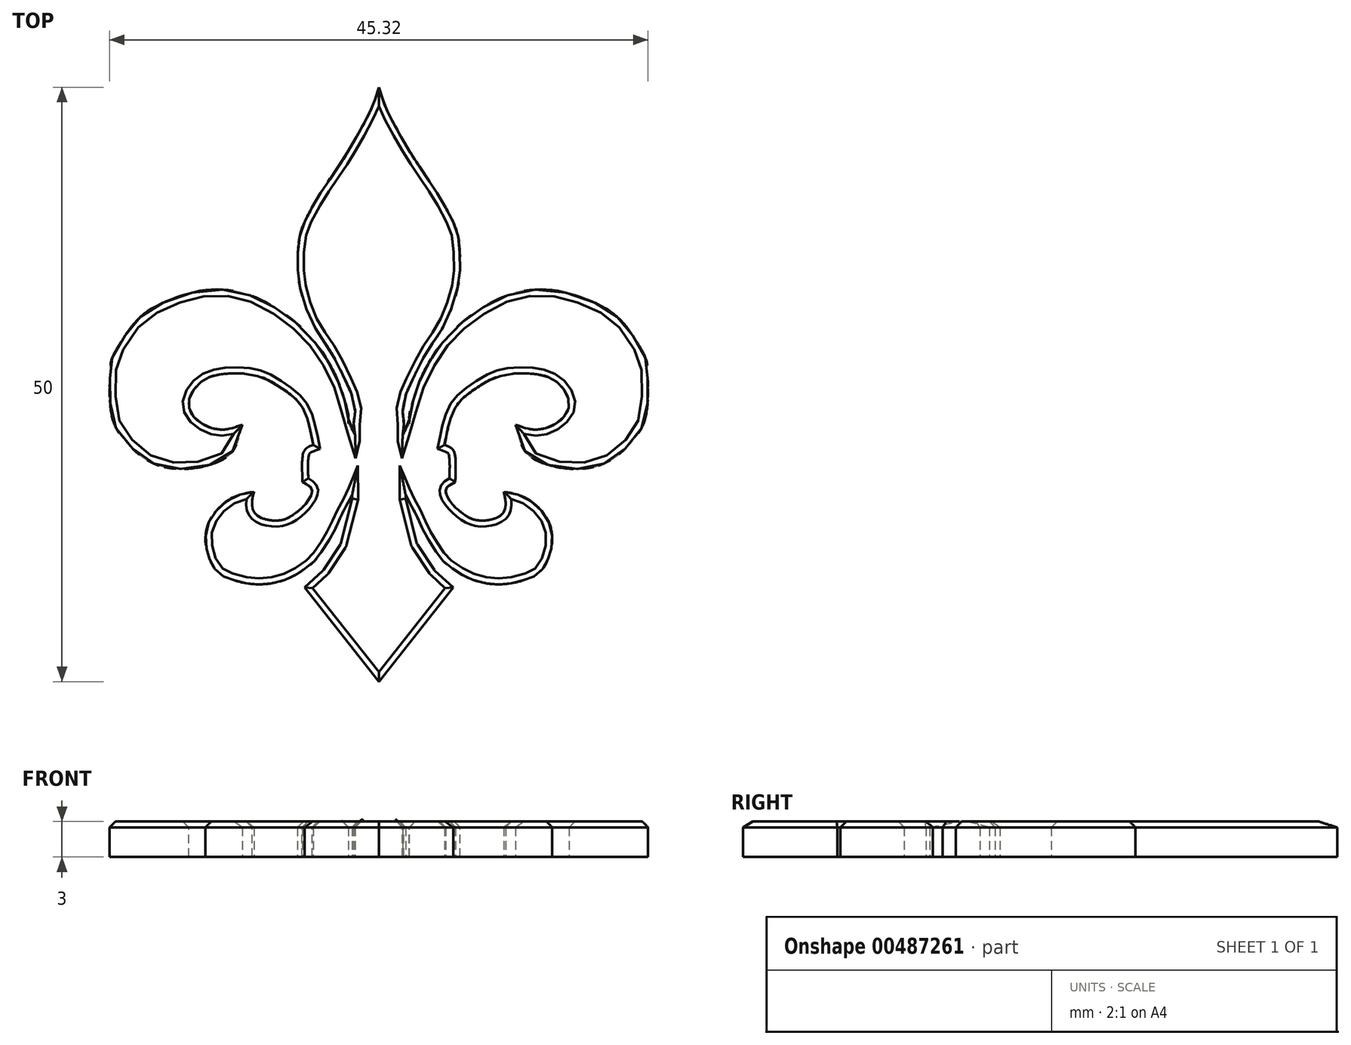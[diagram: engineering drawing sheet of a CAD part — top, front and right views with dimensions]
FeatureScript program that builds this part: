
annotation { "Feature Type Name" : "Feature", "Feature Type Description" : "" }
export const myFeature = defineFeature(function(context is Context, id is Id, definition is map)
    precondition{}
    {
        {
            var Q0;
            Q0=qCreatedBy(makeId("Top.planeOp"),FACE);
            var sketch = newSketch(context, id + "F0", { "sketchPlane" : qUnion([Q0])});
            skFitSpline(sketch, "E0", {"points": [v(11.5, 2.74) * mm, v(13.38, 2.32) * mm, v(15.33, 3.16) * mm, v(16, 4.67) * mm, v(15, 6.3) * mm, v(13.4, 6.96) * mm, v(10.33, 6.88) * mm, v(8.2, 5.81) * mm, v(6.5, 4.3) * mm, v(5.76, 2.22) * mm, v(5.52, 1.03) * mm], "startDerivative": vector(19.3, -6.88) * mm, "endDerivative": vector(-2.82, -13.97) * mm});
            skFitSpline(sketch, "E1", {"points": [v(5.52, 1.03) * mm, v(6.22, 0.64) * mm, v(6.45, -0.33) * mm, v(6.43, -2.09) * mm], "startDerivative": vector(2.93, -1.03) * mm, "endDerivative": vector(-0.17, -4.48) * mm});
            skFitSpline(sketch, "E2", {"points": [v(6.43, -2.09) * mm, v(5.63, -2.72) * mm, v(5.95, -3.63) * mm, v(6.63, -4.4) * mm, v(7.7, -5.13) * mm, v(8.74, -5.33) * mm, v(9.87, -5.1) * mm, v(10.53, -4.56) * mm, v(10.66, -3.7) * mm, v(10.5, -2.9) * mm], "startDerivative": vector(-9.63, -4.74) * mm, "endDerivative": vector(-2.24, 7.58) * mm});
            skFitSpline(sketch, "E3", {"points": [v(11.5, 2.74) * mm, v(12.27, 0.55) * mm, v(13.89, -0.53) * mm, v(16.43, -0.98) * mm, v(18.62, -0.66) * mm, v(20.21, 0.26) * mm, v(21.75, 1.88) * mm, v(22.43, 3.3) * mm, v(22.66, 5.5) * mm, v(22.62, 6.97) * mm, v(22.5, 8.17) * mm, v(21.68, 9.74) * mm, v(20.6, 11.26) * mm, v(19.34, 12.35) * mm, v(17.2, 13.39) * mm, v(14.4, 14.09) * mm, v(11.95, 13.95) * mm, v(9.92, 13.24) * mm, v(8.06, 12.14) * mm, v(6.57, 10.95) * mm, v(5.01, 9.2) * mm, v(4.18, 7.88) * mm, v(3.5, 6.57) * mm, v(3.13, 5.57) * mm, v(2.84, 4.65) * mm, v(2.57, 3.5) * mm, v(2.51, 2.74) * mm, v(2, 1.84) * mm], "startDerivative": vector(14.67, -57.16) * mm, "endDerivative": vector(-10.4, -34.92) * mm});
            skFitSpline(sketch, "E4", {"points": [v(2, 1.84) * mm, v(2.1, 2.74) * mm, v(2, 4.16) * mm, v(3, 6.9) * mm, v(4.22, 9.17) * mm, v(5.48, 11.08) * mm, v(6.66, 14.41) * mm, v(6.83, 16.72) * mm, v(6.61, 18.8) * mm, v(5.94, 20.41) * mm, v(4.88, 22.27) * mm, v(3.75, 23.94) * mm, v(2.72, 25.52) * mm, v(1.54, 27.56) * mm, v(0.82, 28.93) * mm, v(0.42, 29.83) * mm, v(0, 31.12) * mm], "startDerivative": vector(-4.93, 20.4) * mm, "endDerivative": vector(-7.9, 26.17) * mm});
            skFitSpline(sketch, "E5", {"points": [v(10.5, -2.9) * mm, v(12.12, -3.3) * mm, v(13.5, -4.3) * mm, v(14.35, -5.56) * mm, v(14.59, -7.08) * mm, v(14.37, -8.17) * mm, v(14, -9.09) * mm, v(13.3, -9.86) * mm, v(12.33, -10.3) * mm, v(11.2, -10.59) * mm, v(9.94, -10.7) * mm, v(8.46, -10.48) * mm, v(7.29, -10.04) * mm, v(6.42, -9.51) * mm, v(5.49, -8.8) * mm, v(4.78, -7.87) * mm, v(4.05, -6.73) * mm, v(3.45, -5.55) * mm, v(2.93, -4.43) * mm, v(2.25, -3.16) * mm], "startDerivative": vector(27.91, -4.23) * mm, "endDerivative": vector(-9.83, 23.64) * mm});
            skLineSegment(sketch, "E6", {"start": v(2.25, -3.16) * mm, "end": v(2.25, -3.5) * mm});
            skLineSegment(sketch, "E7", {"start": v(2.25, -3.5) * mm, "end": v(3.2, -7.29) * mm});
            skLineSegment(sketch, "E8", {"start": v(3.2, -7.29) * mm, "end": v(4.69, -9.52) * mm});
            skLineSegment(sketch, "E9", {"start": v(4.69, -9.52) * mm, "end": v(6.25, -10.96) * mm});
            skLineSegment(sketch, "E10", {"start": v(6.25, -10.96) * mm, "end": v(0, -18.88) * mm});
            skFitSpline(sketch, "E11.MirrorCS", {"points": [v(-2, 1.84) * mm, v(-2.1, 2.74) * mm, v(-2, 4.16) * mm, v(-3, 6.9) * mm, v(-4.22, 9.17) * mm, v(-5.48, 11.08) * mm, v(-6.66, 14.41) * mm, v(-6.83, 16.72) * mm, v(-6.61, 18.8) * mm, v(-5.94, 20.41) * mm, v(-4.88, 22.27) * mm, v(-3.75, 23.94) * mm, v(-2.72, 25.52) * mm, v(-1.54, 27.56) * mm, v(-0.82, 28.93) * mm, v(-0.42, 29.83) * mm, v(0, 31.12) * mm], "startDerivative": vector(4.93, 20.4) * mm, "endDerivative": vector(7.9, 26.17) * mm});
            skFitSpline(sketch, "E12.MirrorCS", {"points": [v(-11.5, 2.74) * mm, v(-12.27, 0.55) * mm, v(-13.89, -0.53) * mm, v(-16.43, -0.98) * mm, v(-18.62, -0.66) * mm, v(-20.21, 0.26) * mm, v(-21.75, 1.88) * mm, v(-22.43, 3.3) * mm, v(-22.66, 5.5) * mm, v(-22.62, 6.97) * mm, v(-22.5, 8.17) * mm, v(-21.68, 9.74) * mm, v(-20.6, 11.26) * mm, v(-19.34, 12.35) * mm, v(-17.2, 13.39) * mm, v(-14.4, 14.09) * mm, v(-11.95, 13.95) * mm, v(-9.92, 13.24) * mm, v(-8.06, 12.14) * mm, v(-6.57, 10.95) * mm, v(-5.01, 9.2) * mm, v(-4.18, 7.88) * mm, v(-3.5, 6.57) * mm, v(-3.13, 5.57) * mm, v(-2.84, 4.65) * mm, v(-2.57, 3.5) * mm, v(-2.51, 2.74) * mm, v(-2, 1.84) * mm], "startDerivative": vector(-14.67, -57.16) * mm, "endDerivative": vector(10.4, -34.92) * mm});
            skFitSpline(sketch, "E13.MirrorCS", {"points": [v(-11.5, 2.74) * mm, v(-13.38, 2.32) * mm, v(-15.33, 3.16) * mm, v(-16, 4.67) * mm, v(-15, 6.3) * mm, v(-13.4, 6.96) * mm, v(-10.33, 6.88) * mm, v(-8.2, 5.81) * mm, v(-6.5, 4.3) * mm, v(-5.76, 2.22) * mm, v(-5.52, 1.03) * mm], "startDerivative": vector(-19.3, -6.88) * mm, "endDerivative": vector(2.82, -13.97) * mm});
            skFitSpline(sketch, "E14.MirrorCS", {"points": [v(-6.43, -2.09) * mm, v(-5.63, -2.72) * mm, v(-5.95, -3.63) * mm, v(-6.63, -4.4) * mm, v(-7.7, -5.13) * mm, v(-8.74, -5.33) * mm, v(-9.87, -5.1) * mm, v(-10.53, -4.56) * mm, v(-10.66, -3.7) * mm, v(-10.5, -2.9) * mm], "startDerivative": vector(9.63, -4.74) * mm, "endDerivative": vector(2.24, 7.58) * mm});
            skFitSpline(sketch, "E15.MirrorCS", {"points": [v(-10.5, -2.9) * mm, v(-12.12, -3.3) * mm, v(-13.5, -4.3) * mm, v(-14.35, -5.56) * mm, v(-14.59, -7.08) * mm, v(-14.37, -8.17) * mm, v(-14, -9.09) * mm, v(-13.3, -9.86) * mm, v(-12.33, -10.3) * mm, v(-11.2, -10.59) * mm, v(-9.94, -10.7) * mm, v(-8.46, -10.48) * mm, v(-7.29, -10.04) * mm, v(-6.42, -9.51) * mm, v(-5.49, -8.8) * mm, v(-4.78, -7.87) * mm, v(-4.05, -6.73) * mm, v(-3.45, -5.55) * mm, v(-2.93, -4.43) * mm, v(-2.25, -3.16) * mm], "startDerivative": vector(-27.91, -4.23) * mm, "endDerivative": vector(9.83, 23.64) * mm});
            skLineSegment(sketch, "E16.MirrorCS", {"start": v(-3.2, -7.29) * mm, "end": v(-4.69, -9.52) * mm});
            skLineSegment(sketch, "E17.MirrorCS", {"start": v(-2.25, -3.5) * mm, "end": v(-3.2, -7.29) * mm});
            skLineSegment(sketch, "E18.MirrorCS", {"start": v(-4.69, -9.52) * mm, "end": v(-6.25, -10.96) * mm});
            skLineSegment(sketch, "E19.MirrorCS", {"start": v(-6.25, -10.96) * mm, "end": v(0, -18.88) * mm});
            skLineSegment(sketch, "E20.MirrorCS", {"start": v(-2.25, -3.16) * mm, "end": v(-2.25, -3.5) * mm});
            skFitSpline(sketch, "E21.MirrorCS", {"points": [v(-5.52, 1.03) * mm, v(-6.22, 0.64) * mm, v(-6.45, -0.33) * mm, v(-6.43, -2.09) * mm], "startDerivative": vector(-2.93, -1.03) * mm, "endDerivative": vector(0.17, -4.48) * mm});
            skSolve(sketch);
        }
        {
            var Q0;
            Q0=makeQuery(id+"F0.imprint","IMPRINT",FACE,{"disambiguationData":[TD([[makeQuery(id+"F0.imprint","IMPRINT",EDGE,{"derivedFrom":sQuery(id+"F0.wireOp",EDGE,"E0")}),-1.0]])]});
            extrude(context, id + "F1", {"entities" : qUnion([Q0]), "depth" : 3 * mm});
        }
        {
            var Q0;
            Q0=makeQuery(id+"F1.opExtrude","SWEPT_EDGE",EDGE,{"disambiguationData":[OSD([sQuery(id+"F0.wireOp",EDGE,"E16.MirrorCS"),sQuery(id+"F0.wireOp",EDGE,"E17.MirrorCS")])]});
            var Q1;
            Q1=makeQuery(id+"F1.opExtrude","SWEPT_EDGE",EDGE,{"disambiguationData":[OSD([sQuery(id+"F0.wireOp",EDGE,"E16.MirrorCS"),sQuery(id+"F0.wireOp",EDGE,"E18.MirrorCS")])]});
            var Q2;
            Q2=makeQuery(id+"F1.opExtrude","SWEPT_EDGE",EDGE,{"disambiguationData":[OSD([sQuery(id+"F0.wireOp",EDGE,"E8"),sQuery(id+"F0.wireOp",EDGE,"E9")])]});
            var Q3;
            Q3=makeQuery(id+"F1.opExtrude","SWEPT_EDGE",EDGE,{"disambiguationData":[OSD([sQuery(id+"F0.wireOp",EDGE,"E7"),sQuery(id+"F0.wireOp",EDGE,"E8")])]});
            fillet(context, id + "F2", {"entities" : qUnion([Q0, Q1, Q2, Q3]), "radius" : .3 * mm, "tangentPropagation" : true, "allowEdgeOverflow" : false});
        }
        {
            var Q0;
            Q0=makeQuery(id+"F1.opExtrude","CAP_FACE",FACE,{"disambiguationData":[OSD([sQuery(id+"F0.wireOp",EDGE,"E0"),sQuery(id+"F0.wireOp",EDGE,"E1"),sQuery(id+"F0.wireOp",EDGE,"E2"),sQuery(id+"F0.wireOp",EDGE,"E3"),sQuery(id+"F0.wireOp",EDGE,"E4"),sQuery(id+"F0.wireOp",EDGE,"E5"),sQuery(id+"F0.wireOp",EDGE,"E6"),sQuery(id+"F0.wireOp",EDGE,"E7"),sQuery(id+"F0.wireOp",EDGE,"E8"),sQuery(id+"F0.wireOp",EDGE,"E9"),sQuery(id+"F0.wireOp",EDGE,"E10"),sQuery(id+"F0.wireOp",EDGE,"E11.MirrorCS"),sQuery(id+"F0.wireOp",EDGE,"E12.MirrorCS"),sQuery(id+"F0.wireOp",EDGE,"E13.MirrorCS"),sQuery(id+"F0.wireOp",EDGE,"E14.MirrorCS"),sQuery(id+"F0.wireOp",EDGE,"E15.MirrorCS"),sQuery(id+"F0.wireOp",EDGE,"E16.MirrorCS"),sQuery(id+"F0.wireOp",EDGE,"E17.MirrorCS"),sQuery(id+"F0.wireOp",EDGE,"E18.MirrorCS"),sQuery(id+"F0.wireOp",EDGE,"E19.MirrorCS"),sQuery(id+"F0.wireOp",EDGE,"E20.MirrorCS"),sQuery(id+"F0.wireOp",EDGE,"E21.MirrorCS")])],"isStart":false});
            chamfer(context, id + "F3", {"entities" : qUnion([Q0]), "width" : .5 * mm, "tangentPropagation" : true});
        }
    });
